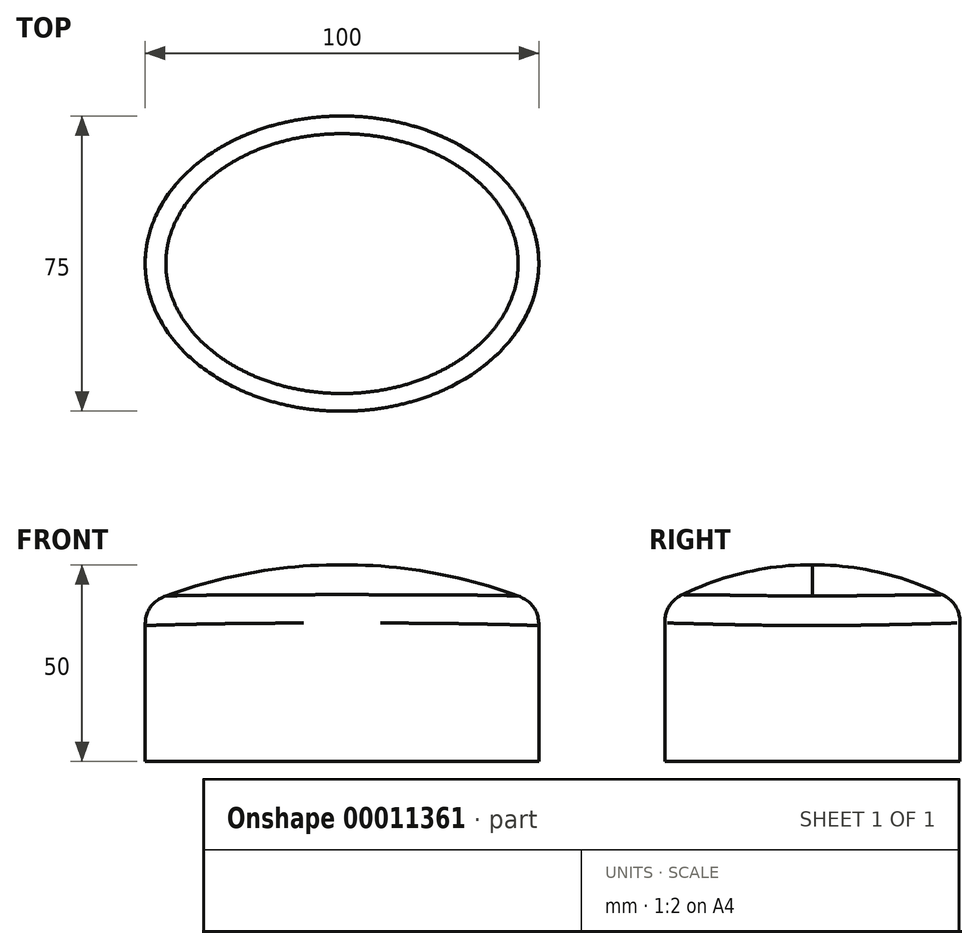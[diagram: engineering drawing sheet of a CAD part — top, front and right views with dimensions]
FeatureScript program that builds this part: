
annotation { "Feature Type Name" : "Feature", "Feature Type Description" : "" }
export const myFeature = defineFeature(function(context is Context, id is Id, definition is map)
    precondition{}
    {
        {
            var Q0;
            Q0=qCreatedBy(makeId("Top.planeOp"),FACE);
            var sketch = newSketch(context, id + "F0", { "sketchPlane" : qUnion([Q0])});
            skLineSegment(sketch, "E0", {"start": v(0, 0) * mm, "end": v(50, 0) * mm, "construction": true});
            skLineSegment(sketch, "E1", {"start": v(0, 0) * mm, "end": v(0, 37.5) * mm, "construction": true});
            skEllipse(sketch, "E2", {"center": v(0, 0) * mm, "majorRadius": 50 * mm, "minorRadius": 37.5 * mm, "majorAxis": v(1, 0)});
            skSolve(sketch);
        }
        {
            var Q0;
            Q0=qCreatedBy(makeId("Front.planeOp"),FACE);
            var sketch = newSketch(context, id + "F1", { "sketchPlane" : qUnion([Q0])});
            skLineSegment(sketch, "E3", {"start": v(0, 0) * mm, "end": v(0, 10) * mm, "construction": true});
            skArc(sketch, "E4", {"start": v(50, 0) * mm, "mid": v(25.5, 7.48) * mm, "end": v(0, 10) * mm});
            skSolve(sketch);
        }
        {
            var Q0;
            Q0=qCreatedBy(makeId("Right.planeOp"),FACE);
            var sketch = newSketch(context, id + "F2", { "sketchPlane" : qUnion([Q0])});
            skLineSegment(sketch, "E5", {"start": v(0, 0) * mm, "end": v(0, 10) * mm, "construction": true});
            skArc(sketch, "E6", {"start": v(37.5, 0) * mm, "mid": v(19.4, 7.46) * mm, "end": v(0, 10) * mm});
            skSolve(sketch);
        }
        {
            var Q0;
            Q0=qCreatedBy(makeId("Front.planeOp"),FACE);
            var sketch = newSketch(context, id + "F3", { "sketchPlane" : qUnion([Q0])});
            skLineSegment(sketch, "E7.0", {"start": v(0, 0) * mm, "end": v(0, 10) * mm, "construction": true});
            skArc(sketch, "E8.0", {"start": v(50, 0) * mm, "mid": v(25.5, 7.48) * mm, "end": v(0, 10) * mm, "construction": true});
            skLineSegment(sketch, "E9", {"start": v(0, 10) * mm, "end": v(0, 0) * mm, "construction": true});
            skArc(sketch, "E10.0.MirrorCS", {"start": v(-50, 0) * mm, "mid": v(-25.5, 7.48) * mm, "end": v(0, 10) * mm});
            skSolve(sketch);
        }
        {
            var Q0;
            Q0=qCreatedBy(makeId("Right.planeOp"),FACE);
            var sketch = newSketch(context, id + "F4", { "sketchPlane" : qUnion([Q0])});
            skArc(sketch, "E11.0", {"start": v(37.5, 0) * mm, "mid": v(19.4, 7.46) * mm, "end": v(0, 10) * mm, "construction": true});
            skLineSegment(sketch, "E11.1", {"start": v(0, 0) * mm, "end": v(0, 10) * mm, "construction": true});
            skArc(sketch, "E12.0.MirrorCS", {"start": v(-37.5, 0) * mm, "mid": v(-19.4, 7.46) * mm, "end": v(0, 10) * mm});
            skSolve(sketch);
        }
        {
            var Q0;
            Q0=sQuery(id+"F1.wireOp",EDGE,"E4");
            var Q1;
            Q1=sQuery(id+"F2.wireOp",EDGE,"E6");
            var Q2;
            Q2=sQuery(id+"F3.wireOp",EDGE,"E10.0.MirrorCS");
            var Q3;
            Q3=sQuery(id+"F4.wireOp",EDGE,"E12.0.MirrorCS");
            var Q4;
            Q4=sQuery(id+"F0.wireOp",EDGE,"E2");
            var Q5;
            Q5=sQuery(id+"F0.wireOp",VERTEX,"E0.end");
            var Q6;
            Q6=sQuery(id+"F4.wireOp",VERTEX,"09f91b4d-dd68-4e11-8c16-2b60e2509cb8.0.start");
            var Q7;
            Q7=sQuery(id+"F3.wireOp",VERTEX,"05837fb8-1f4e-4c1d-a666-7b2030571829.0.MirrorCS.end");
            var Q8;
            Q8=sQuery(id+"F4.wireOp",VERTEX,"074d9ff6-27a1-46a8-9423-f7ec91c35071.0.MirrorCS.end");
            loft(context, id + "F5", {"bodyType" : ExtendedToolBodyType.SURFACE, "addGuides" : true, "wireProfilesArray" : [{ "wireProfileEntities" : qUnion([Q0]) }, { "wireProfileEntities" : qUnion([Q1]) }, { "wireProfileEntities" : qUnion([Q2]) }, { "wireProfileEntities" : qUnion([Q3]) }], "guidesArray" : [{ "guideEntities" : qUnion([Q4]), "guideDerivativeType" : LoftGuideDerivativeType.DEFAULT, "guideDerivativeMagnitude" : 1 }], "connections" : [{ "connectionEntities" : qUnion([Q5, Q6, Q7, Q8]), "connectionEdgeQueries" : qUnion([]), "connectionEdgeParameters" : [] }]});
        }
        {
            var Q0;
            Q0 = qSketchRegion(id + "F0", true);
            var Q1;
            Q1=makeQuery(id+"F5.opLoft","SWEPT_FACE",FACE,{"disambiguationData":[OSD([sQuery(id+"F0.wireOp",EDGE,"E2"),sQuery(id+"F1.wireOp",VERTEX,"E4.end"),sQuery(id+"F1.wireOp",EDGE,"E4"),sQuery(id+"F2.wireOp",VERTEX,"E6.end"),sQuery(id+"F2.wireOp",EDGE,"E6")])]});
            extrude(context, id + "F6", {"entities" : qUnion([Q0]), "endBound" : BoundingType.UP_TO_SURFACE, "endBoundEntityFace" : qUnion([Q1]), "depth" : 25 * mm, "hasSecondDirection" : true, "secondDirectionOppositeDirection" : true, "secondDirectionDepth" : 40 * mm});
        }
        {
            var Q0;
            Q0=makeQuery(id+"F6.opExtrude","CAP_EDGE",EDGE,{"disambiguationData":[OSD([sQuery(id+"F0.wireOp",EDGE,"E2")]),OD(4.0)],"isStart":false});
            fillet(context, id + "F7", {"entities" : qUnion([Q0]), "radius" : 8 * mm, "tangentPropagation" : true, "rho" : 0.5, "crossSection" : FilletCrossSection.CONIC, "allowEdgeOverflow" : false});
        }
    });
